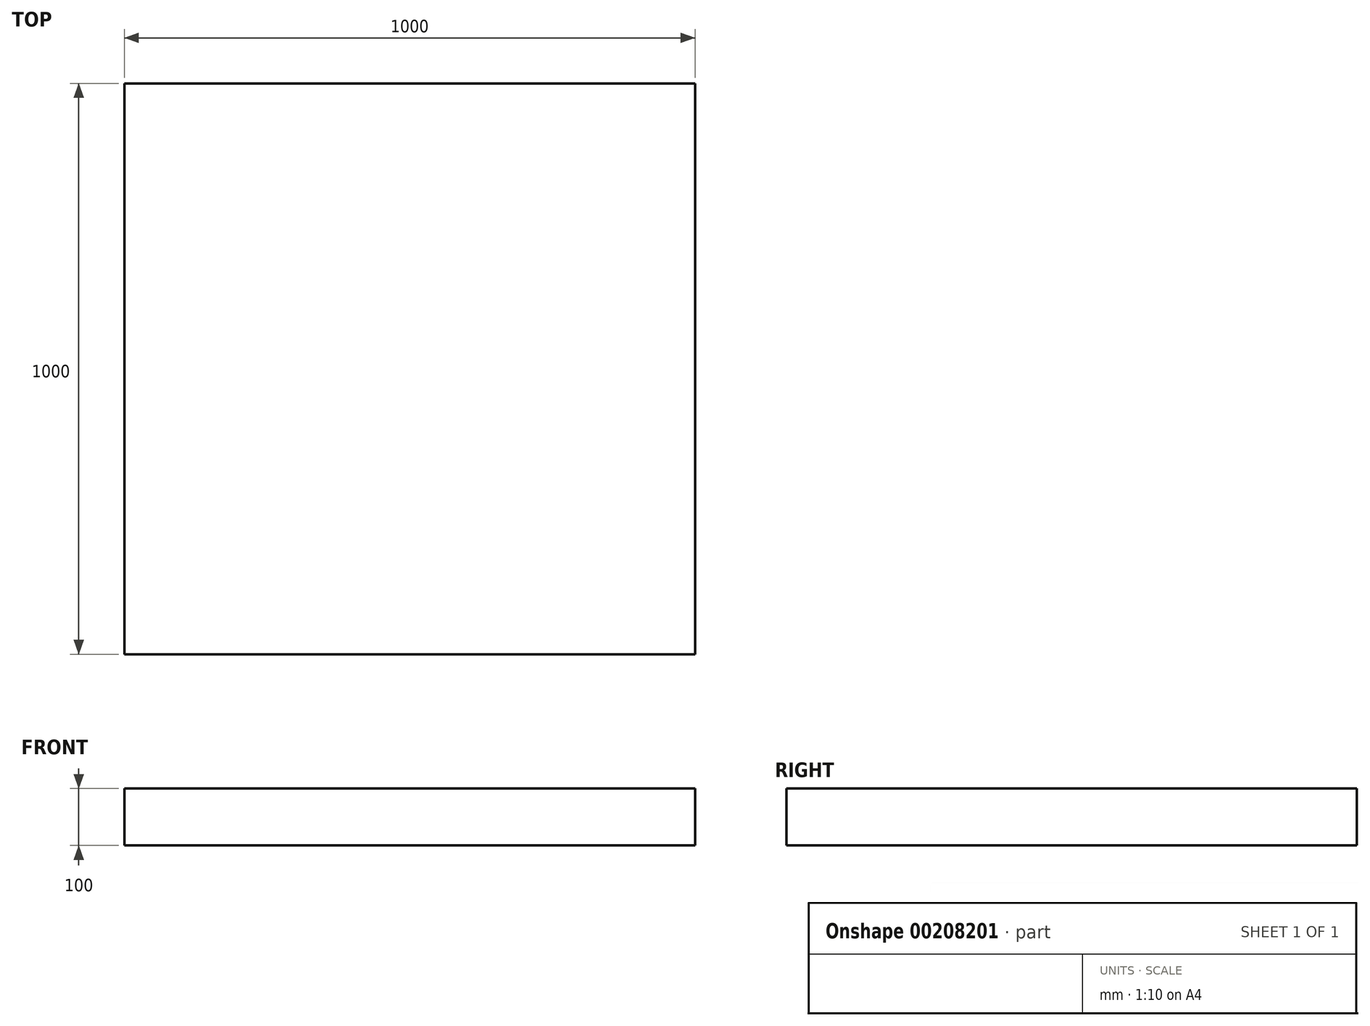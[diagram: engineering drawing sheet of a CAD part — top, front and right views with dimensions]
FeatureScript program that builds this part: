
annotation { "Feature Type Name" : "Feature", "Feature Type Description" : "" }
export const myFeature = defineFeature(function(context is Context, id is Id, definition is map)
    precondition{}
    {
        {
            var Q0;
            Q0=qCreatedBy(makeId("Top.planeOp"),FACE);
            var sketch = newSketch(context, id + "F0", { "sketchPlane" : qUnion([Q0])});
            skLineSegment(sketch, "E0.bottom", {"start": v(-500, 500) * mm, "end": v(500, 500) * mm});
            skLineSegment(sketch, "E0.top", {"start": v(-500, -500) * mm, "end": v(500, -500) * mm});
            skLineSegment(sketch, "E0.left", {"start": v(-500, 500) * mm, "end": v(-500, -500) * mm});
            skLineSegment(sketch, "E0.right", {"start": v(500, 500) * mm, "end": v(500, -500) * mm});
            skSolve(sketch);
        }
        {
            var Q0;
            Q0=makeQuery(id+"F0.imprint","IMPRINT",FACE,{"disambiguationData":[TD([[makeQuery(id+"F0.imprint","IMPRINT",EDGE,{"derivedFrom":sQuery(id+"F0.wireOp",EDGE,"E0.bottom")}),-1.0]])]});
            extrude(context, id + "F1", {"entities" : qUnion([Q0]), "depth" : 100 * mm});
        }
    });
